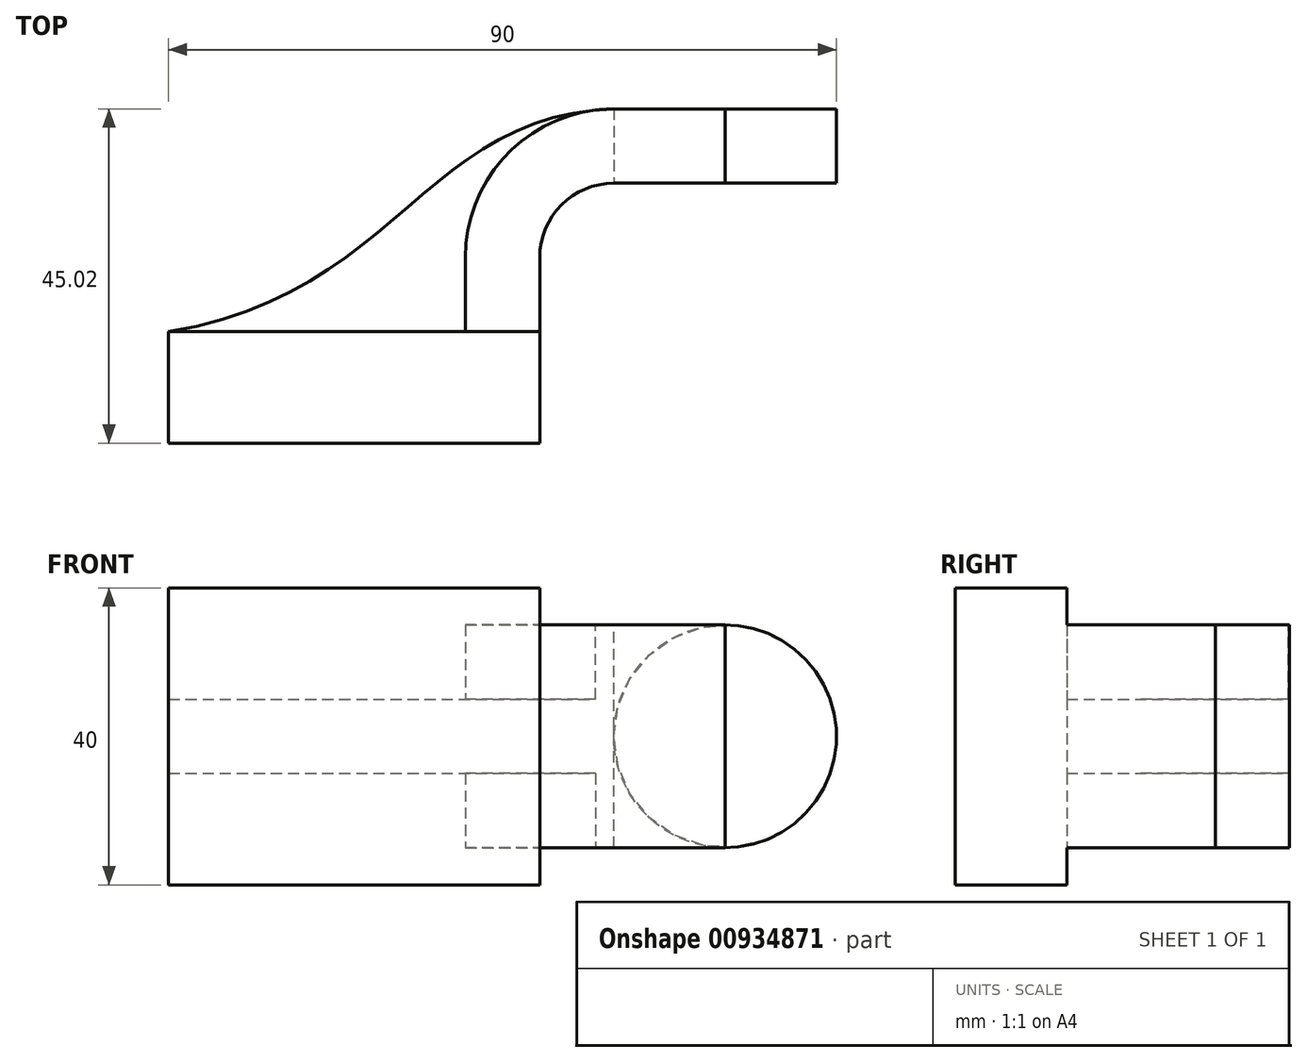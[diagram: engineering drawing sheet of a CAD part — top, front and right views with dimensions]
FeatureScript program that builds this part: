
annotation { "Feature Type Name" : "Feature", "Feature Type Description" : "" }
export const myFeature = defineFeature(function(context is Context, id is Id, definition is map)
    precondition{}
    {
        {
            var Q0;
            Q0=qCreatedBy(makeId("Top.planeOp"),FACE);
            var sketch = newSketch(context, id + "F0", { "sketchPlane" : qUnion([Q0])});
            skLineSegment(sketch, "E0.bottom", {"start": v(-25, 7.5) * mm, "end": v(25, 7.5) * mm});
            skLineSegment(sketch, "E0.top", {"start": v(-25, -7.5) * mm, "end": v(25, -7.5) * mm});
            skLineSegment(sketch, "E0.left", {"start": v(-25, 7.5) * mm, "end": v(-25, -7.5) * mm});
            skLineSegment(sketch, "E0.right", {"start": v(25, 7.5) * mm, "end": v(25, -7.5) * mm});
            skPoint(sketch, "E0.middle", {"position": v(0, 0) * mm});
            skPoint(sketch, "E1.middle", {"position": v(50, 32.5) * mm});
            skLineSegment(sketch, "E2", {"start": v(25, 7.5) * mm, "end": v(25, 17.5) * mm});
            skArc(sketch, "E3", {"start": v(25, 17.5) * mm, "mid": v(27.93, 24.57) * mm, "end": v(35, 27.5) * mm});
            skLineSegment(sketch, "E4", {"start": v(35, 27.5) * mm, "end": v(50, 27.5) * mm});
            skLineSegment(sketch, "E5.0", {"start": v(35, 37.5) * mm, "end": v(50, 37.5) * mm});
            skArc(sketch, "E5.1", {"start": v(15, 17.5) * mm, "mid": v(20.86, 31.64) * mm, "end": v(35, 37.5) * mm});
            skLineSegment(sketch, "E5.2", {"start": v(15, 7.5) * mm, "end": v(15, 17.5) * mm});
            skLineSegment(sketch, "E6", {"start": v(50, 37.5) * mm, "end": v(50, 27.5) * mm});
            skFitSpline(sketch, "E7", {"points": [v(-25, 7.5) * mm, v(35, 37.5) * mm], "startDerivative": vector(93.3, 15.5) * mm, "endDerivative": vector(76.83, 2.4) * mm});
            skLineSegment(sketch, "E8.left", {"start": v(35, 27.5) * mm, "end": v(35, 37.18) * mm});
            skLineSegment(sketch, "E9.bottom", {"start": v(35, 37.5) * mm, "end": v(65, 37.5) * mm});
            skLineSegment(sketch, "E9.top", {"start": v(35, 27.5) * mm, "end": v(65, 27.5) * mm});
            skLineSegment(sketch, "E9.left", {"start": v(35, 37.5) * mm, "end": v(35, 27.5) * mm});
            skLineSegment(sketch, "E9.right", {"start": v(65, 37.5) * mm, "end": v(65, 27.5) * mm});
            skSolve(sketch);
        }
        {
            var Q0;
            Q0=makeQuery(id+"F0.imprint","IMPRINT",FACE,{"disambiguationData":[TD([[makeQuery(id+"F0.imprint","IMPRINT",EDGE,{"derivedFrom":sQuery(id+"F0.wireOp",EDGE,"E0.top")}),1.0]])]});
            extrude(context, id + "F1", {"entities" : qUnion([Q0]), "depth" : 20 * mm, "offsetDistance" : 25 * mm, "hasSecondDirection" : true, "secondDirectionOppositeDirection" : true, "secondDirectionDepth" : 20 * mm});
        }
        {
            var Q0;
            {var subQ0=sQuery(id+"F0.wireOp",EDGE,"E4");Q0=makeQuery(id+"F0.imprint","IMPRINT",FACE,{"disambiguationData":[TD([[makeQuery(id+"F0.imprint","IMPRINT",EDGE,{"derivedFrom":subQ0}),1.0]])]});}
            var Q1;
            {var subQ0=sQuery(id+"F0.wireOp",EDGE,"E2");Q1=makeQuery(id+"F0.imprint","IMPRINT",FACE,{"disambiguationData":[TD([[makeQuery(id+"F0.imprint","IMPRINT",EDGE,{"derivedFrom":subQ0}),1.0]])]});}
            var Q2;
            {var subQ0=sQuery(id+"F0.wireOp",EDGE,"E6");Q2=makeQuery(id+"F0.imprint","IMPRINT",FACE,{"disambiguationData":[TD([[makeQuery(id+"F0.imprint","IMPRINT",EDGE,{"derivedFrom":subQ0}),-1.0]])]});}
            extrude(context, id + "F2", {"entities" : qUnion([Q0, Q1, Q2]), "operationType" : NewBodyOperationType.ADD, "depth" : 15 * mm, "offsetDistance" : 25 * mm, "hasSecondDirection" : true, "secondDirectionOppositeDirection" : true, "secondDirectionDepth" : 15 * mm});
        }
        {
            var Q0;
            {var subQ3=sQuery(id+"F0.wireOp",EDGE,"E5.2");Q0=makeQuery(id+"F0.imprint","IMPRINT",FACE,{"disambiguationData":[TD([[makeQuery(id+"F0.imprint","IMPRINT",EDGE,{"derivedFrom":subQ3}),1.0]])]});}
            extrude(context, id + "F3", {"entities" : qUnion([Q0]), "operationType" : NewBodyOperationType.ADD, "depth" : 5 * mm, "offsetDistance" : 25 * mm, "hasSecondDirection" : true, "secondDirectionOppositeDirection" : true, "secondDirectionDepth" : 5 * mm});
        }
        {
            var Q0;
            {var subQ0=sQuery(id+"F0.wireOp",EDGE,"E6");Q0=makeQuery(id+"F0.imprint","IMPRINT",FACE,{"disambiguationData":[TD([[makeQuery(id+"F0.imprint","IMPRINT",EDGE,{"derivedFrom":subQ0}),1.0]])]});}
            var Q1;
            Q1=sQuery(id+"F0.wireOp",EDGE,"E6");
            revolve(context, id + "F4", {"surfaceOperationType" : NewSurfaceOperationType.NEW, "entities" : qUnion([Q0]), "axis" : qUnion([Q1]), "revolveType" : RevolveType.FULL});
        }
    });
